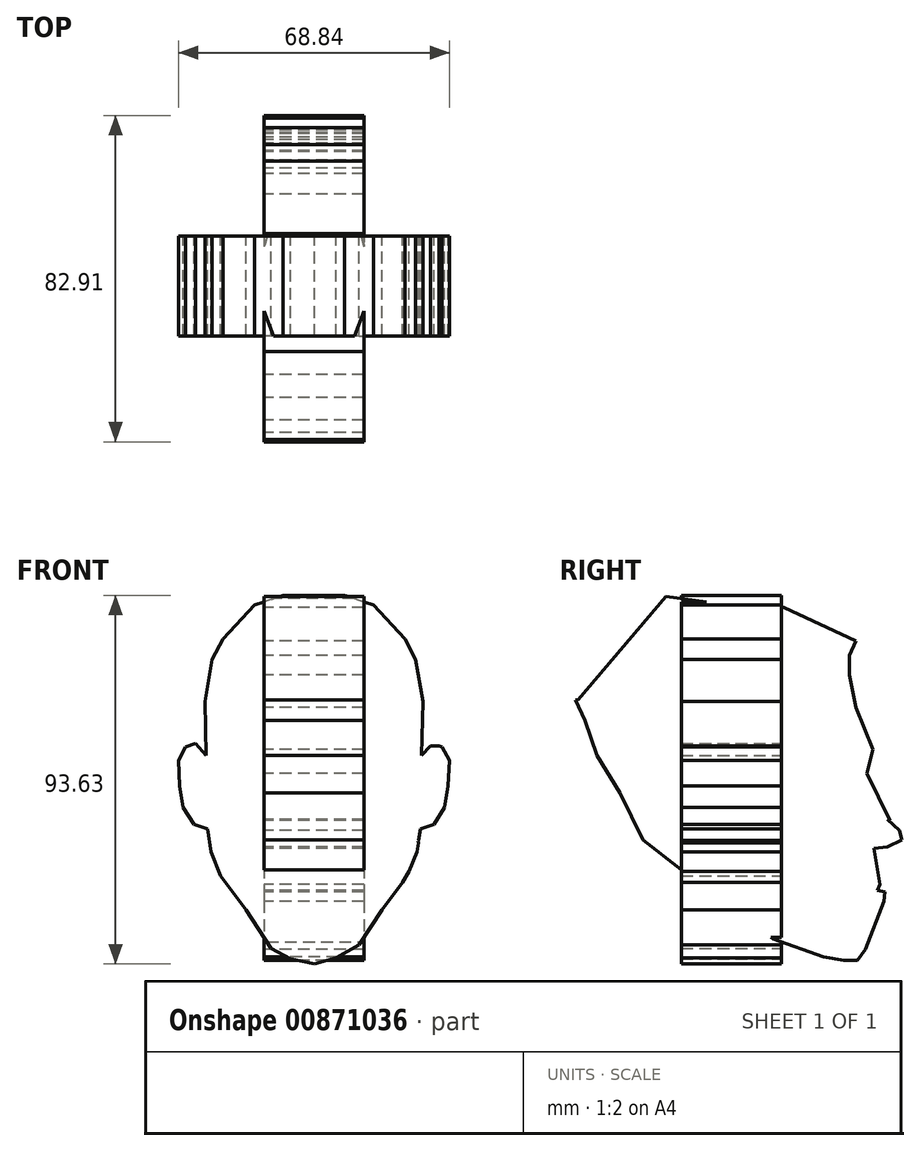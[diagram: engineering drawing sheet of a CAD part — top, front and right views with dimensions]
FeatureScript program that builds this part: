
annotation { "Feature Type Name" : "Feature", "Feature Type Description" : "" }
export const myFeature = defineFeature(function(context is Context, id is Id, definition is map)
    precondition{}
    {
        {
            var Q0;
            Q0=qCreatedBy(makeId("Right.planeOp"),FACE);
            var sketch = newSketch(context, id + "F0", { "sketchPlane" : qUnion([Q0])});
            skLineSegment(sketch, "E0.bottom", {"start": v(-20.96, 36.1) * mm, "end": v(21.57, 36.1) * mm});
            skLineSegment(sketch, "E0.top", {"start": v(-20.96, -18.66) * mm, "end": v(21.57, -18.66) * mm});
            skLineSegment(sketch, "E0.left", {"start": v(-20.96, 36.1) * mm, "end": v(-20.96, -18.66) * mm});
            skLineSegment(sketch, "E0.right", {"start": v(21.57, 36.1) * mm, "end": v(21.57, -18.66) * mm});
            skSolve(sketch);
        }
        {
            var Q0;
            Q0=makeQuery(id+"F0.imprint","IMPRINT",FACE,{"disambiguationData":[TD([[makeQuery(id+"F0.imprint","IMPRINT",EDGE,{"derivedFrom":sQuery(id+"F0.wireOp",EDGE,"E0.bottom")}),-1.0]])]});
            extrude(context, id + "F1", {"entities" : qUnion([Q0]), "depth" : 25.4 * mm, "offsetDistance" : 25.4 * mm});
        }
        {
            var Q0;
            Q0=makeQuery(id+"F1.opExtrude","SWEPT_BODY",BODY,{"disambiguationData":[OSD([sQuery(id+"F0.wireOp",EDGE,"E0.bottom"),sQuery(id+"F0.wireOp",EDGE,"E0.top"),sQuery(id+"F0.wireOp",EDGE,"E0.left"),sQuery(id+"F0.wireOp",EDGE,"E0.right")])]});
            deleteBodies(context, id + "F2", {"entities" : qUnion([Q0])});
        }
        {
            var Q0;
            Q0=qCreatedBy(makeId("Right.planeOp"),FACE);
            var sketch = newSketch(context, id + "F3", { "sketchPlane" : qUnion([Q0])});
            skLineSegment(sketch, "E1", {"start": v(-39.01, 19.89) * mm, "end": v(-16.68, 46.2) * mm});
            skLineSegment(sketch, "E2", {"start": v(-16.68, 46.2) * mm, "end": v(4.74, 43.45) * mm});
            skLineSegment(sketch, "E3", {"start": v(4.74, 43.45) * mm, "end": v(13.3, 43.45) * mm});
            skLineSegment(sketch, "E4", {"start": v(13.3, 43.45) * mm, "end": v(31.67, 34.88) * mm});
            skLineSegment(sketch, "E5", {"start": v(31.67, 34.88) * mm, "end": v(29.95, 31.2) * mm});
            skLineSegment(sketch, "E6", {"start": v(29.95, 31.2) * mm, "end": v(29.95, 26.31) * mm});
            skLineSegment(sketch, "E7", {"start": v(29.95, 26.31) * mm, "end": v(31.67, 18.05) * mm});
            skLineSegment(sketch, "E8", {"start": v(31.67, 18.05) * mm, "end": v(35.95, 7.34) * mm});
            skLineSegment(sketch, "E9", {"start": v(35.95, 7.34) * mm, "end": v(34.42, 1.22) * mm});
            skLineSegment(sketch, "E10", {"start": v(34.42, 1.22) * mm, "end": v(40.23, -10.7) * mm});
            skLineSegment(sketch, "E11", {"start": v(39.62, -10.4) * mm, "end": v(42.68, -13.16) * mm});
            skLineSegment(sketch, "E12", {"start": v(42.68, -13.16) * mm, "end": v(43.3, -15.6) * mm});
            skLineSegment(sketch, "E13", {"start": v(43.3, -15.6) * mm, "end": v(39.62, -17.44) * mm});
            skLineSegment(sketch, "E14", {"start": v(39.62, -17.44) * mm, "end": v(36.26, -17.75) * mm});
            skLineSegment(sketch, "E15", {"start": v(36.26, -17.75) * mm, "end": v(37.79, -26.92) * mm});
            skLineSegment(sketch, "E16", {"start": v(37.79, -26.92) * mm, "end": v(37.17, -28.45) * mm});
            skLineSegment(sketch, "E17", {"start": v(37.17, -28.45) * mm, "end": v(39.01, -28.76) * mm});
            skLineSegment(sketch, "E18", {"start": v(39.01, -28.76) * mm, "end": v(38.7, -31.2) * mm});
            skLineSegment(sketch, "E19", {"start": v(38.7, -31.2) * mm, "end": v(34.12, -43.45) * mm});
            skLineSegment(sketch, "E20", {"start": v(34.12, -43.45) * mm, "end": v(31.97, -46.2) * mm});
            skLineSegment(sketch, "E21", {"start": v(31.97, -46.2) * mm, "end": v(28.6, -46.2) * mm});
            skLineSegment(sketch, "E22", {"start": v(28.6, -46.2) * mm, "end": v(23.4, -45.28) * mm});
            skLineSegment(sketch, "E23", {"start": v(23.4, -45.28) * mm, "end": v(10.56, -40.7) * mm});
            skLineSegment(sketch, "E24", {"start": v(10.56, -40.7) * mm, "end": v(-1.38, -33.04) * mm});
            skLineSegment(sketch, "E25", {"start": v(-1.38, -33.04) * mm, "end": v(-11.17, -24.48) * mm});
            skLineSegment(sketch, "E26", {"start": v(-11.17, -24.48) * mm, "end": v(-22.49, -15.6) * mm});
            skLineSegment(sketch, "E27", {"start": v(-22.49, -15.6) * mm, "end": v(-28.3, -3.67) * mm});
            skLineSegment(sketch, "E28", {"start": v(-28.3, -3.67) * mm, "end": v(-34.12, 5.81) * mm});
            skLineSegment(sketch, "E29", {"start": v(-34.12, 5.81) * mm, "end": v(-37.17, 14.69) * mm});
            skLineSegment(sketch, "E30", {"start": v(-37.17, 14.69) * mm, "end": v(-39.62, 19.89) * mm});
            skLineSegment(sketch, "E31", {"start": v(-39.01, 19.89) * mm, "end": v(-39.62, 19.89) * mm});
            skLineSegment(sketch, "E32", {"start": v(39.62, -10.4) * mm, "end": v(40.23, -10.7) * mm});
            skSolve(sketch);
        }
        {
            var Q0;
            Q0=qCreatedBy(makeId("Front.planeOp"),FACE);
            var sketch = newSketch(context, id + "F4", { "sketchPlane" : qUnion([Q0])});
            skLineSegment(sketch, "E33", {"start": v(-7.8, 46.5) * mm, "end": v(13, 46.5) * mm});
            skLineSegment(sketch, "E34", {"start": v(13, 46.5) * mm, "end": v(24.32, 35.8) * mm});
            skLineSegment(sketch, "E35", {"start": v(24.32, 35.8) * mm, "end": v(27.69, 29.68) * mm});
            skLineSegment(sketch, "E36", {"start": v(27.69, 29.68) * mm, "end": v(27.69, 16.22) * mm});
            skLineSegment(sketch, "E37", {"start": v(27.69, 16.22) * mm, "end": v(27.69, 8.26) * mm});
            skLineSegment(sketch, "E38", {"start": v(27.69, 8.26) * mm, "end": v(32.28, 8.26) * mm});
            skLineSegment(sketch, "E39", {"start": v(32.28, 8.26) * mm, "end": v(35.34, 6.12) * mm});
            skLineSegment(sketch, "E40", {"start": v(35.34, 6.12) * mm, "end": v(35.64, 0) * mm});
            skLineSegment(sketch, "E41", {"start": v(35.64, 0) * mm, "end": v(33.8, -6.43) * mm});
            skLineSegment(sketch, "E42", {"start": v(33.8, -6.43) * mm, "end": v(31.97, -11.01) * mm});
            skLineSegment(sketch, "E43", {"start": v(31.97, -11.01) * mm, "end": v(28.6, -13.77) * mm});
            skLineSegment(sketch, "E44", {"start": v(28.6, -13.77) * mm, "end": v(26.47, -15.91) * mm});
            skLineSegment(sketch, "E45", {"start": v(26.47, -15.91) * mm, "end": v(26.77, -19.28) * mm});
            skLineSegment(sketch, "E46", {"start": v(26.77, -19.28) * mm, "end": v(24.94, -22.34) * mm});
            skLineSegment(sketch, "E47", {"start": v(24.94, -22.34) * mm, "end": v(19.43, -31.51) * mm});
            skLineSegment(sketch, "E48", {"start": v(19.43, -31.51) * mm, "end": v(11.47, -42.22) * mm});
            skLineSegment(sketch, "E49", {"start": v(11.47, -42.22) * mm, "end": v(5.66, -45.59) * mm});
            skLineSegment(sketch, "E50", {"start": v(5.66, -45.59) * mm, "end": v(0.15, -47.12) * mm});
            skLineSegment(sketch, "E51", {"start": v(0.15, -47.12) * mm, "end": v(-5.97, -45.9) * mm});
            skLineSegment(sketch, "E52", {"start": v(-5.97, -45.9) * mm, "end": v(-10.86, -43.14) * mm});
            skLineSegment(sketch, "E53", {"start": v(-10.86, -43.14) * mm, "end": v(-17.29, -33.35) * mm});
            skLineSegment(sketch, "E54", {"start": v(-17.29, -33.35) * mm, "end": v(-23.71, -24.78) * mm});
            skLineSegment(sketch, "E55", {"start": v(-23.71, -24.78) * mm, "end": v(-26.16, -18.66) * mm});
            skLineSegment(sketch, "E56", {"start": v(-26.16, -18.66) * mm, "end": v(-27.08, -12.85) * mm});
            skLineSegment(sketch, "E57", {"start": v(-27.08, -12.85) * mm, "end": v(-30.44, -11.63) * mm});
            skLineSegment(sketch, "E58", {"start": v(-30.44, -11.63) * mm, "end": v(-33.2, -7.34) * mm});
            skLineSegment(sketch, "E59", {"start": v(-33.2, -7.34) * mm, "end": v(-34.12, -1.84) * mm});
            skLineSegment(sketch, "E60", {"start": v(-34.12, -1.84) * mm, "end": v(-34.42, 4.59) * mm});
            skLineSegment(sketch, "E61", {"start": v(-34.42, 4.59) * mm, "end": v(-32.59, 7.96) * mm});
            skLineSegment(sketch, "E62", {"start": v(-32.59, 7.96) * mm, "end": v(-30.14, 8.87) * mm});
            skLineSegment(sketch, "E63", {"start": v(-30.14, 8.87) * mm, "end": v(-27.38, 5.81) * mm});
            skLineSegment(sketch, "E64", {"start": v(-27.38, 5.81) * mm, "end": v(-27.69, 19.58) * mm});
            skLineSegment(sketch, "E65", {"start": v(-27.69, 19.58) * mm, "end": v(-25.85, 30.3) * mm});
            skLineSegment(sketch, "E66", {"start": v(-25.85, 30.3) * mm, "end": v(-23.1, 35.5) * mm});
            skLineSegment(sketch, "E67", {"start": v(-23.1, 35.5) * mm, "end": v(-15.15, 44.06) * mm});
            skLineSegment(sketch, "E68", {"start": v(-15.15, 44.06) * mm, "end": v(-7.8, 46.5) * mm});
            skLineSegment(sketch, "E69.MirrorCS", {"start": v(34.42, 4.59) * mm, "end": v(32.59, 7.96) * mm});
            skLineSegment(sketch, "E70.MirrorCS", {"start": v(34.12, -1.84) * mm, "end": v(34.42, 4.59) * mm});
            skLineSegment(sketch, "E71.MirrorCS", {"start": v(33.2, -7.34) * mm, "end": v(34.12, -1.84) * mm});
            skLineSegment(sketch, "E72.MirrorCS", {"start": v(15.15, 44.06) * mm, "end": v(7.8, 46.5) * mm});
            skLineSegment(sketch, "E73.MirrorCS", {"start": v(30.44, -11.63) * mm, "end": v(33.2, -7.34) * mm});
            skLineSegment(sketch, "E74.MirrorCS", {"start": v(30.14, 8.87) * mm, "end": v(27.38, 5.81) * mm});
            skLineSegment(sketch, "E75.MirrorCS", {"start": v(5.97, -45.9) * mm, "end": v(10.86, -43.14) * mm});
            skLineSegment(sketch, "E76.MirrorCS", {"start": v(25.85, 30.3) * mm, "end": v(23.1, 35.5) * mm});
            skLineSegment(sketch, "E77.MirrorCS", {"start": v(26.16, -18.66) * mm, "end": v(27.08, -12.85) * mm});
            skLineSegment(sketch, "E78.MirrorCS", {"start": v(27.08, -12.85) * mm, "end": v(30.44, -11.63) * mm});
            skLineSegment(sketch, "E79.MirrorCS", {"start": v(23.71, -24.78) * mm, "end": v(26.16, -18.66) * mm});
            skLineSegment(sketch, "E80.MirrorCS", {"start": v(32.59, 7.96) * mm, "end": v(30.14, 8.87) * mm});
            skLineSegment(sketch, "E81.MirrorCS", {"start": v(27.69, 19.58) * mm, "end": v(25.85, 30.3) * mm});
            skLineSegment(sketch, "E82.MirrorCS", {"start": v(27.38, 5.81) * mm, "end": v(27.69, 19.58) * mm});
            skLineSegment(sketch, "E83.MirrorCS", {"start": v(23.1, 35.5) * mm, "end": v(15.15, 44.06) * mm});
            skLineSegment(sketch, "E84.MirrorCS", {"start": v(17.29, -33.35) * mm, "end": v(23.71, -24.78) * mm});
            skLineSegment(sketch, "E85.MirrorCS", {"start": v(10.86, -43.14) * mm, "end": v(17.29, -33.35) * mm});
            skSolve(sketch);
        }
        {
            var Q0;
            {var subQ22=sQuery(id+"F4.wireOp",EDGE,"E50");Q0=makeQuery(id+"F4.imprint","IMPRINT",FACE,{"disambiguationData":[TD([[makeQuery(id+"F4.imprint","IMPRINT",EDGE,{"derivedFrom":subQ22}),-1.0]])]});}
            extrude(context, id + "F5", {"entities" : qUnion([Q0]), "endBound" : BoundingType.SYMMETRIC, "depth" : 25.4 * mm, "offsetDistance" : 25.4 * mm});
        }
        {
            var Q0;
            Q0=makeQuery(id+"F3.imprint","IMPRINT",FACE,{"disambiguationData":[TD([[makeQuery(id+"F3.imprint","IMPRINT",EDGE,{"derivedFrom":sQuery(id+"F3.wireOp",EDGE,"E1")}),-1.0]])]});
            extrude(context, id + "F6", {"entities" : qUnion([Q0]), "operationType" : NewBodyOperationType.ADD, "endBound" : BoundingType.SYMMETRIC, "depth" : 25.4 * mm, "offsetDistance" : 25.4 * mm});
        }
    });
